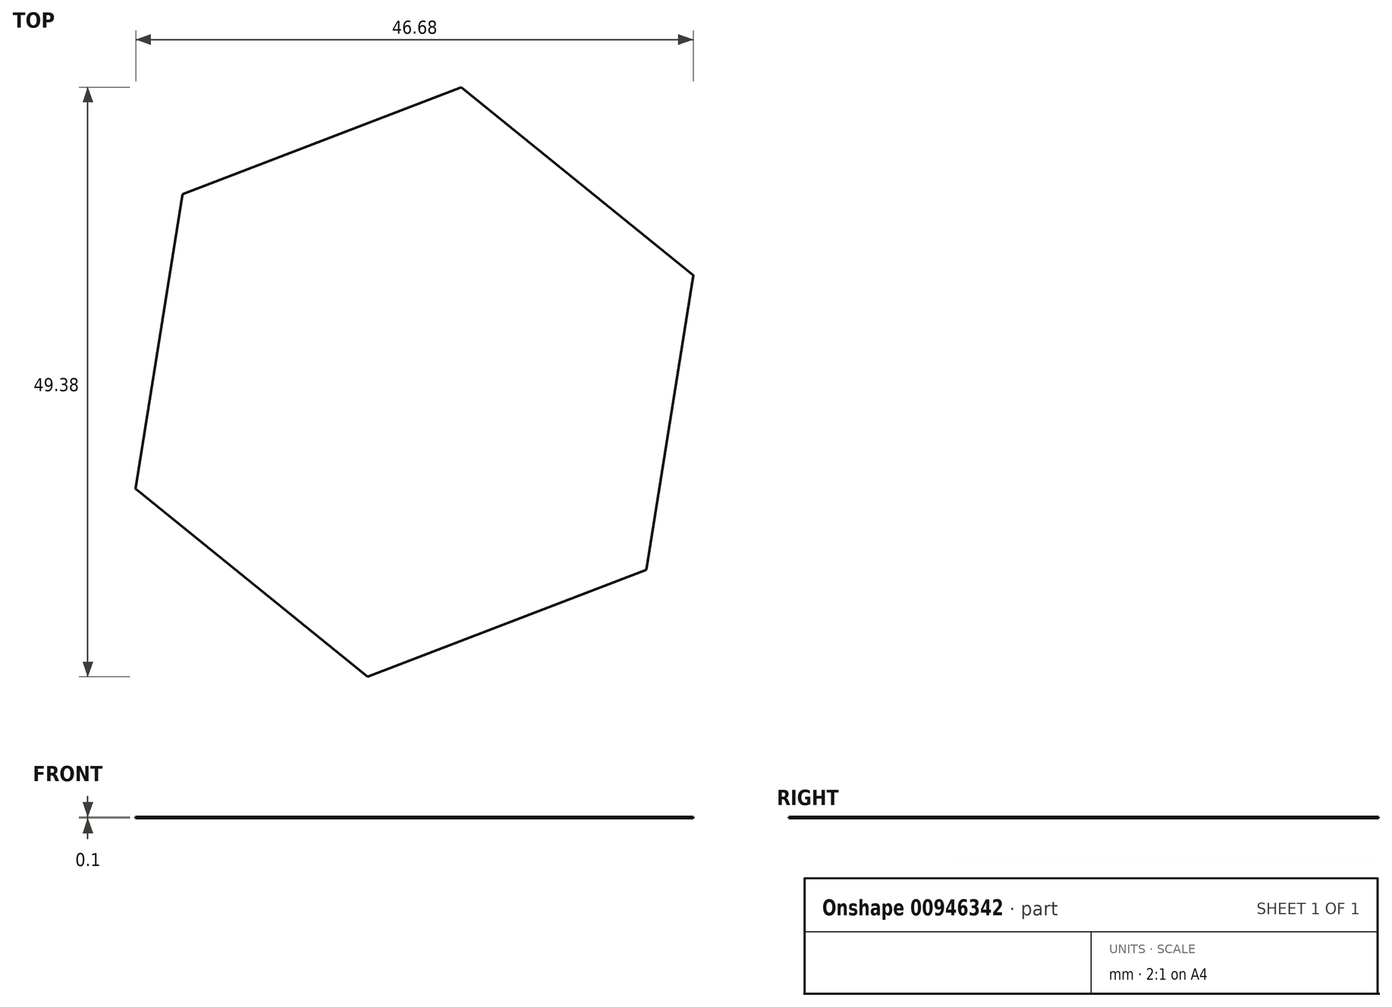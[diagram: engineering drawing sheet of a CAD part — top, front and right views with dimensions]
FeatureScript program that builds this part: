
annotation { "Feature Type Name" : "Feature", "Feature Type Description" : "" }
export const myFeature = defineFeature(function(context is Context, id is Id, definition is map)
    precondition{}
    {
        {
            var Q0;
            Q0=qCreatedBy(makeId("Top.planeOp"),FACE);
            var sketch = newSketch(context, id + "F0", { "sketchPlane" : qUnion([Q0])});
            skCircle(sketch, "E0.cCircle", {"center": v(0, 0) * mm, "radius": 21.65 * mm, "construction": true});
            skLineSegment(sketch, "E0.0", {"start": v(19.42, -15.74) * mm, "end": v(-3.92, -24.7) * mm});
            skLineSegment(sketch, "E0.1", {"start": v(-3.92, -24.7) * mm, "end": v(-23.34, -8.95) * mm});
            skLineSegment(sketch, "E0.2", {"start": v(-23.34, -8.95) * mm, "end": v(-19.42, 15.74) * mm});
            skLineSegment(sketch, "E0.3", {"start": v(-19.42, 15.74) * mm, "end": v(3.92, 24.7) * mm});
            skLineSegment(sketch, "E0.4", {"start": v(3.92, 24.7) * mm, "end": v(23.34, 8.95) * mm});
            skLineSegment(sketch, "E0.5", {"start": v(23.34, 8.95) * mm, "end": v(19.42, -15.74) * mm});
            skPoint(sketch, "E0.0.midPoint", {"position": v(7.75, -20.22) * mm});
            skSolve(sketch);
        }
        {
            var Q0;
            Q0=makeQuery(id+"F0.imprint","IMPRINT",FACE,{"disambiguationData":[TD([[makeQuery(id+"F0.imprint","IMPRINT",EDGE,{"derivedFrom":sQuery(id+"F0.wireOp",EDGE,"E0.0")}),-1.0]])]});
            extrude(context, id + "F1", {"entities" : qUnion([Q0]), "depth" : 0.1 * mm, "offsetDistance" : 25 * mm});
        }
    });
